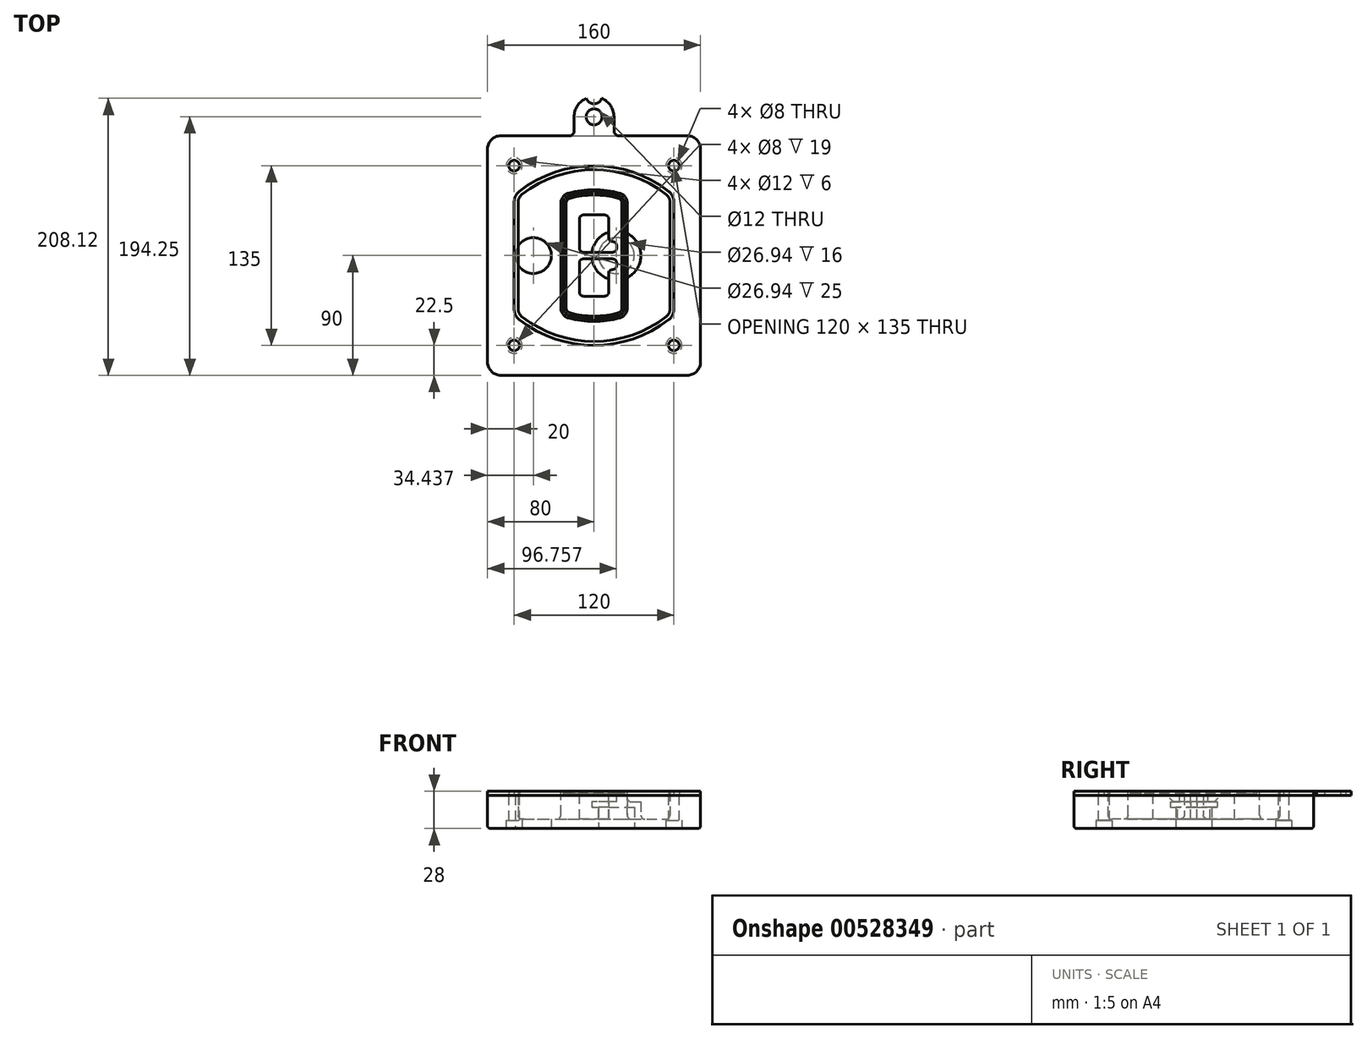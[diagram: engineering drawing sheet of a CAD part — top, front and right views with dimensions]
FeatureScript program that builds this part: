
annotation { "Feature Type Name" : "Feature", "Feature Type Description" : "" }
export const myFeature = defineFeature(function(context is Context, id is Id, definition is map)
    precondition{}
    {
        {
            var Q0;
            Q0=qCreatedBy(makeId("Top.planeOp"),FACE);
            var sketch = newSketch(context, id + "F0", { "sketchPlane" : qUnion([Q0])});
            skPoint(sketch, "E0.rect.middle", {"position": v(0, 0) * mm});
            skLineSegment(sketch, "E1.bottom", {"start": v(-70, -90) * mm, "end": v(70, -90) * mm});
            skLineSegment(sketch, "E1.top", {"start": v(-70, 90) * mm, "end": v(70, 90) * mm});
            skLineSegment(sketch, "E1.left", {"start": v(-80, -80) * mm, "end": v(-80, 80) * mm});
            skLineSegment(sketch, "E1.right", {"start": v(80, -80) * mm, "end": v(80, 80) * mm});
            skLineSegment(sketch, "E2", {"start": v(-80, 90) * mm, "end": v(80, -90) * mm, "construction": true});
            skLineSegment(sketch, "E3", {"start": v(80, 90) * mm, "end": v(-80, -90) * mm, "construction": true});
            skCircle(sketch, "E4", {"center": v(-60, 67.5) * mm, "radius": 4 * mm});
            skCircle(sketch, "E5", {"center": v(60, 67.5) * mm, "radius": 4 * mm});
            skCircle(sketch, "E6", {"center": v(60, -67.5) * mm, "radius": 4 * mm});
            skCircle(sketch, "E7", {"center": v(-60, -67.5) * mm, "radius": 4 * mm});
            skLineSegment(sketch, "E8", {"start": v(-60, 67.5) * mm, "end": v(60, 67.5) * mm, "construction": true});
            skLineSegment(sketch, "E9", {"start": v(60, 67.5) * mm, "end": v(60, -67.5) * mm, "construction": true});
            skLineSegment(sketch, "E10", {"start": v(60, -67.5) * mm, "end": v(-60, -67.5) * mm, "construction": true});
            skLineSegment(sketch, "E11", {"start": v(-60, -67.5) * mm, "end": v(-60, 67.5) * mm, "construction": true});
            skLineSegment(sketch, "E12", {"start": v(-60, 40.3) * mm, "end": v(-60, -40.3) * mm});
            skLineSegment(sketch, "E13", {"start": v(60, 40.3) * mm, "end": v(60, -40.3) * mm});
            skArc(sketch, "E14", {"start": v(56.15, 48.18) * mm, "mid": v(0, 67.5) * mm, "end": v(-56.15, 48.18) * mm});
            skArc(sketch, "E15", {"start": v(-56.15, -48.18) * mm, "mid": v(0, -67.5) * mm, "end": v(56.15, -48.18) * mm});
            skLineSegment(sketch, "E16", {"start": v(-60, 0) * mm, "end": v(60, 0) * mm, "construction": true});
            skPoint(sketch, "E17.visualSharp", {"position": v(-60, -45) * mm});
            skArc(sketch, "E17.filletArc", {"start": v(-60, -40.3) * mm, "mid": v(-58.99, -44.68) * mm, "end": v(-56.15, -48.18) * mm});
            skPoint(sketch, "E18.visualSharp", {"position": v(-60, 45) * mm});
            skArc(sketch, "E18.filletArc", {"start": v(-56.15, 48.18) * mm, "mid": v(-58.99, 44.68) * mm, "end": v(-60, 40.3) * mm});
            skPoint(sketch, "E19.visualSharp", {"position": v(60, 45) * mm});
            skArc(sketch, "E19.filletArc", {"start": v(60, 40.3) * mm, "mid": v(58.99, 44.68) * mm, "end": v(56.15, 48.18) * mm});
            skPoint(sketch, "E20.visualSharp", {"position": v(60, -45) * mm});
            skArc(sketch, "E20.filletArc", {"start": v(56.15, -48.18) * mm, "mid": v(58.99, -44.68) * mm, "end": v(60, -40.3) * mm});
            skPoint(sketch, "E21.visualSharp", {"position": v(-80, 90) * mm});
            skArc(sketch, "E21.filletArc", {"start": v(-70, 90) * mm, "mid": v(-77.07, 87.07) * mm, "end": v(-80, 80) * mm});
            skPoint(sketch, "E22.visualSharp", {"position": v(80, 90) * mm});
            skArc(sketch, "E22.filletArc", {"start": v(80, 80) * mm, "mid": v(77.07, 87.07) * mm, "end": v(70, 90) * mm});
            skPoint(sketch, "E23.visualSharp", {"position": v(80, -90) * mm});
            skArc(sketch, "E23.filletArc", {"start": v(70, -90) * mm, "mid": v(77.07, -87.07) * mm, "end": v(80, -80) * mm});
            skPoint(sketch, "E24.visualSharp", {"position": v(-80, -90) * mm});
            skArc(sketch, "E24.filletArc", {"start": v(-80, -80) * mm, "mid": v(-77.07, -87.07) * mm, "end": v(-70, -90) * mm});
            skArc(sketch, "E25.0", {"start": v(57, 40.3) * mm, "mid": v(56.3, 43.36) * mm, "end": v(54.3, 45.81) * mm});
            skLineSegment(sketch, "E25.1", {"start": v(57, 40.3) * mm, "end": v(57, -40.3) * mm});
            skArc(sketch, "E25.2", {"start": v(54.3, -45.81) * mm, "mid": v(56.3, -43.36) * mm, "end": v(57, -40.3) * mm});
            skArc(sketch, "E25.3", {"start": v(-54.3, -45.81) * mm, "mid": v(0, -64.5) * mm, "end": v(54.3, -45.81) * mm});
            skArc(sketch, "E25.4", {"start": v(-57, -40.3) * mm, "mid": v(-56.3, -43.36) * mm, "end": v(-54.3, -45.81) * mm});
            skArc(sketch, "E25.5", {"start": v(54.3, 45.81) * mm, "mid": v(0, 64.5) * mm, "end": v(-54.3, 45.81) * mm});
            skLineSegment(sketch, "E25.6", {"start": v(-57, 40.3) * mm, "end": v(-57, -40.3) * mm});
            skArc(sketch, "E25.7", {"start": v(-54.3, 45.81) * mm, "mid": v(-56.3, 43.36) * mm, "end": v(-57, 40.3) * mm});
            skArc(sketch, "E26.0", {"start": v(-58.62, 51.33) * mm, "mid": v(-62.58, 46.43) * mm, "end": v(-64, 40.3) * mm});
            skArc(sketch, "E26.1", {"start": v(58.62, 51.33) * mm, "mid": v(0, 71.5) * mm, "end": v(-58.62, 51.33) * mm});
            skArc(sketch, "E26.2", {"start": v(64, 40.3) * mm, "mid": v(62.58, 46.43) * mm, "end": v(58.62, 51.33) * mm});
            skLineSegment(sketch, "E26.3", {"start": v(64, 40.3) * mm, "end": v(64, -40.3) * mm});
            skArc(sketch, "E26.4", {"start": v(58.62, -51.33) * mm, "mid": v(62.58, -46.43) * mm, "end": v(64, -40.3) * mm});
            skLineSegment(sketch, "E26.5", {"start": v(-64, 40.3) * mm, "end": v(-64, -40.3) * mm});
            skArc(sketch, "E26.6", {"start": v(-58.62, -51.33) * mm, "mid": v(0, -71.5) * mm, "end": v(58.62, -51.33) * mm});
            skArc(sketch, "E26.7", {"start": v(-64, -40.3) * mm, "mid": v(-62.58, -46.43) * mm, "end": v(-58.62, -51.33) * mm});
            skSolve(sketch);
        }
        {
            var Q0;
            Q0=makeQuery(id+"F0.imprint","IMPRINT",FACE,{"disambiguationData":[TD([[makeQuery(id+"F0.imprint","IMPRINT",EDGE,{"derivedFrom":sQuery(id+"F0.wireOp",EDGE,"E1.bottom")}),1.0]])]});
            var Q1;
            Q1=makeQuery(id+"F0.imprint","IMPRINT",FACE,{"disambiguationData":[TD([[makeQuery(id+"F0.imprint","IMPRINT",EDGE,{"derivedFrom":sQuery(id+"F0.wireOp",EDGE,"E12")}),1.0]])]});
            var Q2;
            Q2=makeQuery(id+"F0.imprint","IMPRINT",FACE,{"disambiguationData":[TD([[makeQuery(id+"F0.imprint","IMPRINT",EDGE,{"derivedFrom":sQuery(id+"F0.wireOp",EDGE,"E25.0")}),1.0]])]});
            var Q3;
            Q3=makeQuery(id+"F0.imprint","IMPRINT",FACE,{"disambiguationData":[TD([[makeQuery(id+"F0.imprint","IMPRINT",EDGE,{"derivedFrom":sQuery(id+"F0.wireOp",EDGE,"E12")}),-1.0]])]});
            extrude(context, id + "F1", {"entities" : qUnion([Q0, Q1, Q2, Q3]), "oppositeDirection" : true, "depth" : 25 * mm});
        }
        {
            var Q0;
            Q0=makeQuery(id+"F0.imprint","IMPRINT",FACE,{"disambiguationData":[TD([[makeQuery(id+"F0.imprint","IMPRINT",EDGE,{"derivedFrom":sQuery(id+"F0.wireOp",EDGE,"E12")}),1.0]])]});
            extrude(context, id + "F2", {"entities" : qUnion([Q0]), "operationType" : NewBodyOperationType.ADD, "depth" : 3 * mm});
        }
        {
            var Q0;
            Q0=makeQuery(id+"F0.imprint","IMPRINT",FACE,{"disambiguationData":[TD([[makeQuery(id+"F0.imprint","IMPRINT",EDGE,{"derivedFrom":sQuery(id+"F0.wireOp",EDGE,"E25.0")}),1.0]])]});
            extrude(context, id + "F3", {"entities" : qUnion([Q0]), "operationType" : NewBodyOperationType.REMOVE, "oppositeDirection" : true, "depth" : 18 * mm});
        }
        {
            var Q0;
            Q0=makeQuery(id+"F2.opExtrude","CAP_FACE",FACE,{"disambiguationData":[OSD([sQuery(id+"F0.wireOp",EDGE,"E12"),sQuery(id+"F0.wireOp",EDGE,"E13"),sQuery(id+"F0.wireOp",EDGE,"E14"),sQuery(id+"F0.wireOp",EDGE,"E15"),sQuery(id+"F0.wireOp",EDGE,"E17.filletArc"),sQuery(id+"F0.wireOp",EDGE,"E18.filletArc"),sQuery(id+"F0.wireOp",EDGE,"E19.filletArc"),sQuery(id+"F0.wireOp",EDGE,"E20.filletArc"),sQuery(id+"F0.wireOp",EDGE,"E25.0"),sQuery(id+"F0.wireOp",EDGE,"E25.1"),sQuery(id+"F0.wireOp",EDGE,"E25.2"),sQuery(id+"F0.wireOp",EDGE,"E25.3"),sQuery(id+"F0.wireOp",EDGE,"E25.4"),sQuery(id+"F0.wireOp",EDGE,"E25.5"),sQuery(id+"F0.wireOp",EDGE,"E25.6"),sQuery(id+"F0.wireOp",EDGE,"E25.7")])],"isStart":false});
            var sketch = newSketch(context, id + "F4", { "sketchPlane" : qUnion([Q0])});
            skArc(sketch, "E27.0", {"start": v(-19.08, -46.97) * mm, "mid": v(0, -49.5) * mm, "end": v(19.08, -46.97) * mm});
            skArc(sketch, "E28.0", {"start": v(19.08, 46.97) * mm, "mid": v(0, 49.5) * mm, "end": v(-19.08, 46.97) * mm});
            skLineSegment(sketch, "E29", {"start": v(-25, 39.25) * mm, "end": v(-25, -39.25) * mm});
            skLineSegment(sketch, "E30", {"start": v(25, 39.25) * mm, "end": v(25, -39.25) * mm});
            skLineSegment(sketch, "E31", {"start": v(-25, 45.1) * mm, "end": v(25, 45.1) * mm, "construction": true});
            skLineSegment(sketch, "E32", {"start": v(-25, -45.1) * mm, "end": v(25, -45.1) * mm, "construction": true});
            skPoint(sketch, "E33.visualSharp", {"position": v(-25, 45.1) * mm});
            skArc(sketch, "E33.filletArc", {"start": v(-19.08, 46.97) * mm, "mid": v(-23.35, 44.11) * mm, "end": v(-25, 39.25) * mm});
            skPoint(sketch, "E34.visualSharp", {"position": v(25, 45.1) * mm});
            skArc(sketch, "E34.filletArc", {"start": v(25, 39.25) * mm, "mid": v(23.35, 44.11) * mm, "end": v(19.08, 46.97) * mm});
            skPoint(sketch, "E35.visualSharp", {"position": v(25, -45.1) * mm});
            skArc(sketch, "E35.filletArc", {"start": v(19.08, -46.97) * mm, "mid": v(23.35, -44.11) * mm, "end": v(25, -39.25) * mm});
            skPoint(sketch, "E36.visualSharp", {"position": v(-25, -45.1) * mm});
            skArc(sketch, "E36.filletArc", {"start": v(-25, -39.25) * mm, "mid": v(-23.35, -44.11) * mm, "end": v(-19.08, -46.97) * mm});
            skArc(sketch, "E37.0", {"start": v(54.3, 45.81) * mm, "mid": v(0, 64.5) * mm, "end": v(-54.3, 45.81) * mm});
            skArc(sketch, "E37.1", {"start": v(-54.3, 45.81) * mm, "mid": v(-56.3, 43.36) * mm, "end": v(-57, 40.3) * mm});
            skLineSegment(sketch, "E37.2", {"start": v(-57, 40.3) * mm, "end": v(-57, -40.3) * mm});
            skArc(sketch, "E37.3", {"start": v(-57, -40.3) * mm, "mid": v(-56.3, -43.36) * mm, "end": v(-54.3, -45.81) * mm});
            skArc(sketch, "E37.4", {"start": v(-54.3, -45.81) * mm, "mid": v(0, -64.5) * mm, "end": v(54.3, -45.81) * mm});
            skArc(sketch, "E37.5", {"start": v(54.3, -45.81) * mm, "mid": v(56.3, -43.36) * mm, "end": v(57, -40.3) * mm});
            skLineSegment(sketch, "E37.6", {"start": v(57, 40.3) * mm, "end": v(57, -40.3) * mm});
            skArc(sketch, "E37.7", {"start": v(57, 40.3) * mm, "mid": v(56.3, 43.36) * mm, "end": v(54.3, 45.81) * mm});
            skLineSegment(sketch, "E38.0", {"start": v(23, 39.25) * mm, "end": v(23, -39.25) * mm});
            skArc(sketch, "E38.1", {"start": v(18.56, -45.04) * mm, "mid": v(21.76, -42.9) * mm, "end": v(23, -39.25) * mm});
            skArc(sketch, "E38.2", {"start": v(-18.56, -45.04) * mm, "mid": v(0, -47.5) * mm, "end": v(18.56, -45.04) * mm});
            skArc(sketch, "E38.3", {"start": v(-23, -39.25) * mm, "mid": v(-21.76, -42.9) * mm, "end": v(-18.56, -45.04) * mm});
            skLineSegment(sketch, "E38.4", {"start": v(-23, 39.25) * mm, "end": v(-23, -39.25) * mm});
            skArc(sketch, "E38.5", {"start": v(23, 39.25) * mm, "mid": v(21.76, 42.9) * mm, "end": v(18.56, 45.04) * mm});
            skArc(sketch, "E38.6", {"start": v(-18.56, 45.04) * mm, "mid": v(-21.76, 42.9) * mm, "end": v(-23, 39.25) * mm});
            skArc(sketch, "E38.7", {"start": v(18.56, 45.04) * mm, "mid": v(0, 47.5) * mm, "end": v(-18.56, 45.04) * mm});
            skArc(sketch, "E39.0", {"start": v(21, 39.25) * mm, "mid": v(20.18, 41.68) * mm, "end": v(18.04, 43.1) * mm});
            skLineSegment(sketch, "E39.1", {"start": v(21, 39.25) * mm, "end": v(21, -39.25) * mm});
            skArc(sketch, "E39.2", {"start": v(18.04, -43.1) * mm, "mid": v(20.18, -41.68) * mm, "end": v(21, -39.25) * mm});
            skArc(sketch, "E39.3", {"start": v(-18.04, -43.1) * mm, "mid": v(0, -45.5) * mm, "end": v(18.04, -43.1) * mm});
            skArc(sketch, "E39.4", {"start": v(-21, -39.25) * mm, "mid": v(-20.18, -41.68) * mm, "end": v(-18.04, -43.1) * mm});
            skArc(sketch, "E39.5", {"start": v(18.04, 43.1) * mm, "mid": v(0, 45.5) * mm, "end": v(-18.04, 43.1) * mm});
            skLineSegment(sketch, "E39.6", {"start": v(-21, 39.25) * mm, "end": v(-21, -39.25) * mm});
            skArc(sketch, "E39.7", {"start": v(-18.04, 43.1) * mm, "mid": v(-20.18, 41.68) * mm, "end": v(-21, 39.25) * mm});
            skLineSegment(sketch, "E40", {"start": v(-25, 0) * mm, "end": v(25, 0) * mm, "construction": true});
            skLineSegment(sketch, "E41", {"start": v(-11, 5.5) * mm, "end": v(-11, 27.5) * mm});
            skLineSegment(sketch, "E42", {"start": v(-8, 30.5) * mm, "end": v(8, 30.5) * mm});
            skLineSegment(sketch, "E43", {"start": v(11, 27.5) * mm, "end": v(11, 13.5) * mm});
            skLineSegment(sketch, "E44", {"start": v(14, 10.5) * mm, "end": v(14, 10.5) * mm});
            skLineSegment(sketch, "E45", {"start": v(17, 7.5) * mm, "end": v(17, 5.5) * mm});
            skLineSegment(sketch, "E46", {"start": v(14, 2.5) * mm, "end": v(-8, 2.5) * mm});
            skPoint(sketch, "E47.visualSharp", {"position": v(-11, 30.5) * mm});
            skArc(sketch, "E47.filletArc", {"start": v(-8, 30.5) * mm, "mid": v(-10.12, 29.62) * mm, "end": v(-11, 27.5) * mm});
            skPoint(sketch, "E48.visualSharp", {"position": v(11, 30.5) * mm});
            skArc(sketch, "E48.filletArc", {"start": v(11, 27.5) * mm, "mid": v(10.12, 29.62) * mm, "end": v(8, 30.5) * mm});
            skPoint(sketch, "E49.visualSharp", {"position": v(11, 10.5) * mm});
            skArc(sketch, "E49.filletArc", {"start": v(11, 13.5) * mm, "mid": v(11.88, 11.38) * mm, "end": v(14, 10.5) * mm});
            skPoint(sketch, "E50.visualSharp", {"position": v(17, 10.5) * mm});
            skArc(sketch, "E50.filletArc", {"start": v(17, 7.5) * mm, "mid": v(16.12, 9.62) * mm, "end": v(14, 10.5) * mm});
            skPoint(sketch, "E51.visualSharp", {"position": v(17, 2.5) * mm});
            skArc(sketch, "E51.filletArc", {"start": v(14, 2.5) * mm, "mid": v(16.12, 3.38) * mm, "end": v(17, 5.5) * mm});
            skPoint(sketch, "E52.visualSharp", {"position": v(-11, 2.5) * mm});
            skArc(sketch, "E52.filletArc", {"start": v(-11, 5.5) * mm, "mid": v(-10.12, 3.38) * mm, "end": v(-8, 2.5) * mm});
            skLineSegment(sketch, "E53.0.MirrorCS", {"start": v(14, -2.5) * mm, "end": v(-8, -2.5) * mm});
            skArc(sketch, "E54.0.MirrorCS", {"start": v(-11, -5.5) * mm, "mid": v(-10.12, -3.38) * mm, "end": v(-8, -2.5) * mm});
            skLineSegment(sketch, "E55.0.MirrorCS", {"start": v(-11, -5.5) * mm, "end": v(-11, -27.5) * mm});
            skArc(sketch, "E56.0.MirrorCS", {"start": v(-8, -30.5) * mm, "mid": v(-10.12, -29.62) * mm, "end": v(-11, -27.5) * mm});
            skLineSegment(sketch, "E57.0.MirrorCS", {"start": v(-8, -30.5) * mm, "end": v(8, -30.5) * mm});
            skArc(sketch, "E58.0.MirrorCS", {"start": v(11, -27.5) * mm, "mid": v(10.12, -29.62) * mm, "end": v(8, -30.5) * mm});
            skLineSegment(sketch, "E59.0.MirrorCS", {"start": v(11, -27.5) * mm, "end": v(11, -13.5) * mm});
            skArc(sketch, "E60.0.MirrorCS", {"start": v(11, -13.5) * mm, "mid": v(11.88, -11.38) * mm, "end": v(14, -10.5) * mm});
            skArc(sketch, "E61.0.MirrorCS", {"start": v(17, -7.5) * mm, "mid": v(16.12, -9.62) * mm, "end": v(14, -10.5) * mm});
            skLineSegment(sketch, "E62.0.MirrorCS", {"start": v(17, -7.5) * mm, "end": v(17, -5.5) * mm});
            skArc(sketch, "E63.0.MirrorCS", {"start": v(14, -2.5) * mm, "mid": v(16.12, -3.38) * mm, "end": v(17, -5.5) * mm});
            skSolve(sketch);
        }
        {
            var Q0;
            Q0=makeQuery(id+"F4.imprint","IMPRINT",FACE,{"disambiguationData":[TD([[makeQuery(id+"F4.imprint","IMPRINT",EDGE,{"derivedFrom":sQuery(id+"F4.wireOp",EDGE,"E27.0")}),1.0]])]});
            var Q1;
            Q1=makeQuery(id+"F4.imprint","IMPRINT",FACE,{"disambiguationData":[TD([[makeQuery(id+"F4.imprint","IMPRINT",EDGE,{"derivedFrom":sQuery(id+"F4.wireOp",EDGE,"E38.0")}),-1.0]])]});
            var Q2;
            Q2=makeQuery(id+"F4.imprint","IMPRINT",FACE,{"disambiguationData":[TD([[makeQuery(id+"F4.imprint","IMPRINT",EDGE,{"derivedFrom":sQuery(id+"F4.wireOp",EDGE,"E39.0")}),1.0]])]});
            extrude(context, id + "F5", {"entities" : qUnion([Q0, Q1, Q2]), "operationType" : NewBodyOperationType.ADD, "endBound" : BoundingType.UP_TO_NEXT, "oppositeDirection" : true, "depth" : 25 * mm});
        }
        {
            var Q0;
            Q0=makeQuery(id+"F4.imprint","IMPRINT",FACE,{"disambiguationData":[TD([[makeQuery(id+"F4.imprint","IMPRINT",EDGE,{"derivedFrom":sQuery(id+"F4.wireOp",EDGE,"E38.0")}),-1.0]])]});
            extrude(context, id + "F6", {"entities" : qUnion([Q0]), "operationType" : NewBodyOperationType.REMOVE, "oppositeDirection" : true, "depth" : 2 * mm});
        }
        {
            var Q0;
            Q0=makeQuery(id+"F1.opExtrude","CAP_FACE",FACE,{"disambiguationData":[OSD([sQuery(id+"F0.wireOp",EDGE,"E1.bottom"),sQuery(id+"F0.wireOp",EDGE,"E1.top"),sQuery(id+"F0.wireOp",EDGE,"E1.left"),sQuery(id+"F0.wireOp",EDGE,"E1.right"),sQuery(id+"F0.wireOp",EDGE,"E4"),sQuery(id+"F0.wireOp",EDGE,"E5"),sQuery(id+"F0.wireOp",EDGE,"E6"),sQuery(id+"F0.wireOp",EDGE,"E7"),sQuery(id+"F0.wireOp",EDGE,"E21.filletArc"),sQuery(id+"F0.wireOp",EDGE,"E22.filletArc"),sQuery(id+"F0.wireOp",EDGE,"E23.filletArc"),sQuery(id+"F0.wireOp",EDGE,"E24.filletArc")])],"isStart":false});
            var sketch = newSketch(context, id + "F7", { "sketchPlane" : qUnion([Q0])});
            skCircle(sketch, "E64", {"center": v(16.76, 0) * mm, "radius": 13.47 * mm});
            skCircle(sketch, "E65", {"center": v(-45.56, 0) * mm, "radius": 13.47 * mm});
            skLineSegment(sketch, "E66", {"start": v(80, 0) * mm, "end": v(-80, 0) * mm});
            skCircle(sketch, "E67", {"center": v(16.76, 0) * mm, "radius": 18.47 * mm});
            skCircle(sketch, "E68", {"center": v(60, -67.5) * mm, "radius": 6 * mm});
            skCircle(sketch, "E69", {"center": v(-60, -67.5) * mm, "radius": 6 * mm});
            skCircle(sketch, "E70", {"center": v(-60, 67.5) * mm, "radius": 6 * mm});
            skCircle(sketch, "E71", {"center": v(60, 67.5) * mm, "radius": 6 * mm});
            skSolve(sketch);
        }
        {
            var Q0;
            {var subQ1=sQuery(id+"F7.wireOp",EDGE,"E66");var subQ4=sQuery(id+"F7.wireOp",EDGE,"E64");var subQ6=makeQuery(id+"F7.imprint","INTERSECT",VERTEX,{"disambiguationData":[OD(0.0)],"derivedFrom":[subQ4,subQ1]});Q0=makeQuery(id+"F7.imprint","IMPRINT",FACE,{"disambiguationData":[TD([[makeQuery(id+"F7.imprint","IMPRINT",EDGE,{"disambiguationData":[TD([[subQ6,-1.0]])],"derivedFrom":subQ4}),-1.0]])]});}
            var Q1;
            {var subQ0=sQuery(id+"F7.wireOp",EDGE,"E66");var subQ1=sQuery(id+"F7.wireOp",EDGE,"E64");var subQ3=makeQuery(id+"F7.imprint","INTERSECT",VERTEX,{"disambiguationData":[OD(0.0)],"derivedFrom":[subQ1,subQ0]});Q1=makeQuery(id+"F7.imprint","IMPRINT",FACE,{"disambiguationData":[TD([[makeQuery(id+"F7.imprint","IMPRINT",EDGE,{"disambiguationData":[TD([[subQ3,-1.0]])],"derivedFrom":subQ1}),1.0]])]});}
            var Q2;
            {var subQ0=sQuery(id+"F7.wireOp",EDGE,"E66");var subQ1=sQuery(id+"F7.wireOp",EDGE,"E64");var subQ3=makeQuery(id+"F7.imprint","INTERSECT",VERTEX,{"disambiguationData":[OD(0.0)],"derivedFrom":[subQ1,subQ0]});Q2=makeQuery(id+"F7.imprint","IMPRINT",FACE,{"disambiguationData":[TD([[makeQuery(id+"F7.imprint","IMPRINT",EDGE,{"disambiguationData":[TD([[subQ3,1.0]])],"derivedFrom":subQ1}),1.0]])]});}
            var Q3;
            {var subQ1=sQuery(id+"F7.wireOp",EDGE,"E66");var subQ4=sQuery(id+"F7.wireOp",EDGE,"E64");var subQ6=makeQuery(id+"F7.imprint","INTERSECT",VERTEX,{"disambiguationData":[OD(0.0)],"derivedFrom":[subQ4,subQ1]});Q3=makeQuery(id+"F7.imprint","IMPRINT",FACE,{"disambiguationData":[TD([[makeQuery(id+"F7.imprint","IMPRINT",EDGE,{"disambiguationData":[TD([[subQ6,1.0]])],"derivedFrom":subQ4}),-1.0]])]});}
            extrude(context, id + "F8", {"entities" : qUnion([Q0, Q1, Q2, Q3]), "operationType" : NewBodyOperationType.ADD, "oppositeDirection" : true, "depth" : 20 * mm});
        }
        {
            var Q0;
            {var subQ0=sQuery(id+"F7.wireOp",EDGE,"E66");var subQ1=sQuery(id+"F7.wireOp",EDGE,"E64");var subQ3=makeQuery(id+"F7.imprint","INTERSECT",VERTEX,{"disambiguationData":[OD(0.0)],"derivedFrom":[subQ1,subQ0]});Q0=makeQuery(id+"F7.imprint","IMPRINT",FACE,{"disambiguationData":[TD([[makeQuery(id+"F7.imprint","IMPRINT",EDGE,{"disambiguationData":[TD([[subQ3,-1.0]])],"derivedFrom":subQ1}),1.0]])]});}
            var Q1;
            {var subQ0=sQuery(id+"F7.wireOp",EDGE,"E66");var subQ1=sQuery(id+"F7.wireOp",EDGE,"E64");var subQ3=makeQuery(id+"F7.imprint","INTERSECT",VERTEX,{"disambiguationData":[OD(0.0)],"derivedFrom":[subQ1,subQ0]});Q1=makeQuery(id+"F7.imprint","IMPRINT",FACE,{"disambiguationData":[TD([[makeQuery(id+"F7.imprint","IMPRINT",EDGE,{"disambiguationData":[TD([[subQ3,1.0]])],"derivedFrom":subQ1}),1.0]])]});}
            extrude(context, id + "F9", {"entities" : qUnion([Q0, Q1]), "operationType" : NewBodyOperationType.REMOVE, "oppositeDirection" : true, "depth" : 16 * mm});
        }
        {
            var Q0;
            {var subQ0=sQuery(id+"F7.wireOp",EDGE,"E66");var subQ1=sQuery(id+"F7.wireOp",EDGE,"E65");var subQ3=makeQuery(id+"F7.imprint","INTERSECT",VERTEX,{"disambiguationData":[OD(0.0)],"derivedFrom":[subQ1,subQ0]});Q0=makeQuery(id+"F7.imprint","IMPRINT",FACE,{"disambiguationData":[TD([[makeQuery(id+"F7.imprint","IMPRINT",EDGE,{"disambiguationData":[TD([[subQ3,-1.0]])],"derivedFrom":subQ1}),1.0]])]});}
            var Q1;
            {var subQ0=sQuery(id+"F7.wireOp",EDGE,"E66");var subQ1=sQuery(id+"F7.wireOp",EDGE,"E65");var subQ3=makeQuery(id+"F7.imprint","INTERSECT",VERTEX,{"disambiguationData":[OD(0.0)],"derivedFrom":[subQ1,subQ0]});Q1=makeQuery(id+"F7.imprint","IMPRINT",FACE,{"disambiguationData":[TD([[makeQuery(id+"F7.imprint","IMPRINT",EDGE,{"disambiguationData":[TD([[subQ3,1.0]])],"derivedFrom":subQ1}),1.0]])]});}
            extrude(context, id + "F10", {"entities" : qUnion([Q0, Q1]), "operationType" : NewBodyOperationType.REMOVE, "oppositeDirection" : true, "depth" : 25 * mm});
        }
        {
            var Q0;
            Q0=makeQuery(id+"F7.imprint","IMPRINT",FACE,{"disambiguationData":[TD([[makeQuery(id+"F7.imprint","IMPRINT",EDGE,{"derivedFrom":sQuery(id+"F7.wireOp",EDGE,"E68")}),1.0]])]});
            var Q1;
            Q1=makeQuery(id+"F7.imprint","IMPRINT",FACE,{"disambiguationData":[TD([[makeQuery(id+"F7.imprint","IMPRINT",EDGE,{"derivedFrom":makeQuery(id+"F1.opExtrude","CAP_EDGE",EDGE,{"disambiguationData":[OSD([sQuery(id+"F0.wireOp",EDGE,"E5")])],"isStart":false})}),-1.0]])]});
            var Q2;
            Q2=makeQuery(id+"F7.imprint","IMPRINT",FACE,{"disambiguationData":[TD([[makeQuery(id+"F7.imprint","IMPRINT",EDGE,{"derivedFrom":sQuery(id+"F7.wireOp",EDGE,"E69")}),1.0]])]});
            var Q3;
            Q3=makeQuery(id+"F7.imprint","IMPRINT",FACE,{"disambiguationData":[TD([[makeQuery(id+"F7.imprint","IMPRINT",EDGE,{"derivedFrom":makeQuery(id+"F1.opExtrude","CAP_EDGE",EDGE,{"disambiguationData":[OSD([sQuery(id+"F0.wireOp",EDGE,"E4")])],"isStart":false})}),-1.0]])]});
            var Q4;
            Q4=makeQuery(id+"F7.imprint","IMPRINT",FACE,{"disambiguationData":[TD([[makeQuery(id+"F7.imprint","IMPRINT",EDGE,{"derivedFrom":sQuery(id+"F7.wireOp",EDGE,"E70")}),1.0]])]});
            var Q5;
            Q5=makeQuery(id+"F7.imprint","IMPRINT",FACE,{"disambiguationData":[TD([[makeQuery(id+"F7.imprint","IMPRINT",EDGE,{"derivedFrom":makeQuery(id+"F1.opExtrude","CAP_EDGE",EDGE,{"disambiguationData":[OSD([sQuery(id+"F0.wireOp",EDGE,"E7")])],"isStart":false})}),-1.0]])]});
            var Q6;
            Q6=makeQuery(id+"F7.imprint","IMPRINT",FACE,{"disambiguationData":[TD([[makeQuery(id+"F7.imprint","IMPRINT",EDGE,{"derivedFrom":sQuery(id+"F7.wireOp",EDGE,"E71")}),1.0]])]});
            var Q7;
            Q7=makeQuery(id+"F7.imprint","IMPRINT",FACE,{"disambiguationData":[TD([[makeQuery(id+"F7.imprint","IMPRINT",EDGE,{"derivedFrom":makeQuery(id+"F1.opExtrude","CAP_EDGE",EDGE,{"disambiguationData":[OSD([sQuery(id+"F0.wireOp",EDGE,"E6")])],"isStart":false})}),-1.0]])]});
            extrude(context, id + "F11", {"entities" : qUnion([Q0, Q1, Q2, Q3, Q4, Q5, Q6, Q7]), "operationType" : NewBodyOperationType.REMOVE, "oppositeDirection" : true, "depth" : 6 * mm});
        }
        {
            var Q0;
            Q0=makeQuery(id+"F9.boolean.opBoolean","COPY",FACE,{"derivedFrom":makeQuery(id+"F9.opExtrude","CAP_FACE",FACE,{"disambiguationData":[OSD([sQuery(id+"F7.wireOp",EDGE,"E64")])],"isStart":false})});
            var sketch = newSketch(context, id + "F12", { "sketchPlane" : qUnion([Q0])});
            skArc(sketch, "E72.0", {"start": v(11, 17.55) * mm, "mid": v(2.57, 11.82) * mm, "end": v(-1.54, 2.5) * mm});
            skArc(sketch, "E72.1", {"start": v(-1.54, -2.5) * mm, "mid": v(2.57, -11.82) * mm, "end": v(11, -17.55) * mm});
            skLineSegment(sketch, "E73", {"start": v(-1.54, -2.5) * mm, "end": v(14, -2.5) * mm});
            skLineSegment(sketch, "E74.0", {"start": v(14, 2.5) * mm, "end": v(-1.54, 2.5) * mm});
            skArc(sketch, "E74.1", {"start": v(14, 2.5) * mm, "mid": v(16.12, 3.38) * mm, "end": v(17, 5.5) * mm});
            skLineSegment(sketch, "E74.2", {"start": v(17, 7.5) * mm, "end": v(17, 5.5) * mm});
            skArc(sketch, "E74.3", {"start": v(17, 7.5) * mm, "mid": v(16.12, 9.62) * mm, "end": v(14, 10.5) * mm});
            skArc(sketch, "E74.4", {"start": v(11, 13.5) * mm, "mid": v(11.88, 11.38) * mm, "end": v(14, 10.5) * mm});
            skLineSegment(sketch, "E74.5", {"start": v(11, 17.55) * mm, "end": v(11, 13.5) * mm});
            skLineSegment(sketch, "E74.7", {"start": v(14, -2.5) * mm, "end": v(-1.54, -2.5) * mm});
            skArc(sketch, "E74.8", {"start": v(14, -2.5) * mm, "mid": v(16.12, -3.38) * mm, "end": v(17, -5.5) * mm});
            skLineSegment(sketch, "E74.9", {"start": v(17, -7.5) * mm, "end": v(17, -5.5) * mm});
            skArc(sketch, "E74.10", {"start": v(17, -7.5) * mm, "mid": v(16.12, -9.62) * mm, "end": v(14, -10.5) * mm});
            skArc(sketch, "E74.11", {"start": v(11, -13.5) * mm, "mid": v(11.88, -11.38) * mm, "end": v(14, -10.5) * mm});
            skLineSegment(sketch, "E74.12", {"start": v(11, -17.55) * mm, "end": v(11, -13.5) * mm});
            skPoint(sketch, "E75.orphan", {"position": v(11, -27.5) * mm});
            skPoint(sketch, "E76.orphan", {"position": v(-8, -2.5) * mm});
            skPoint(sketch, "E77.orphan", {"position": v(-8, 2.5) * mm});
            skPoint(sketch, "E78.orphan", {"position": v(11, 27.5) * mm});
            skSolve(sketch);
        }
        {
            var Q0;
            {var subQ7=sQuery(id+"F12.wireOp",EDGE,"E72.0");var subQ14=sQuery(id+"F12.wireOp",EDGE,"E72.1");var subQ16=sQuery(id+"F12.wireOp",EDGE,"E74.1");var subQ18=sQuery(id+"F12.wireOp",EDGE,"E74.8");Q0=qUnion([makeQuery(id+"F12.imprint","IMPRINT",FACE,{"disambiguationData":[TD([[makeQuery(id+"F12.imprint","IMPRINT",EDGE,{"derivedFrom":subQ7}),1.0]])]}),makeQuery(id+"F12.imprint","IMPRINT",FACE,{"disambiguationData":[TD([[makeQuery(id+"F12.imprint","IMPRINT",EDGE,{"derivedFrom":subQ14}),1.0]])]}),makeQuery(id+"F12.imprint","IMPRINT",FACE,{"disambiguationData":[TD([[makeQuery(id+"F12.imprint","IMPRINT",EDGE,{"derivedFrom":subQ16}),1.0]])]}),makeQuery(id+"F12.imprint","IMPRINT",FACE,{"disambiguationData":[TD([[makeQuery(id+"F12.imprint","IMPRINT",EDGE,{"derivedFrom":subQ18}),-1.0]])]})]);}
            var Q1;
            Q1=makeQuery(id+"F5.boolean.opBoolean","SPLIT",FACE,{"disambiguationData":[TD([makeQuery(id+"F5.opExtrude","SWEPT_FACE",FACE,{"disambiguationData":[OSD([sQuery(id+"F4.wireOp",EDGE,"E41")])]})])],"derivedFrom":makeQuery(id+"F3.boolean.opBoolean","COPY",FACE,{"derivedFrom":makeQuery(id+"F3.opExtrude","CAP_FACE",FACE,{"disambiguationData":[OSD([sQuery(id+"F0.wireOp",EDGE,"E25.0"),sQuery(id+"F0.wireOp",EDGE,"E25.1"),sQuery(id+"F0.wireOp",EDGE,"E25.2"),sQuery(id+"F0.wireOp",EDGE,"E25.3"),sQuery(id+"F0.wireOp",EDGE,"E25.4"),sQuery(id+"F0.wireOp",EDGE,"E25.5"),sQuery(id+"F0.wireOp",EDGE,"E25.6"),sQuery(id+"F0.wireOp",EDGE,"E25.7")])],"isStart":false})})});
            extrude(context, id + "F13", {"entities" : qUnion([Q0]), "operationType" : NewBodyOperationType.REMOVE, "endBound" : BoundingType.UP_TO_SURFACE, "endBoundEntityFace" : qUnion([Q1]), "depth" : 25 * mm});
        }
        {
            var Q0;
            Q0=makeQuery(id+"F3.boolean.opBoolean","COPY",EDGE,{"derivedFrom":makeQuery(id+"F3.opExtrude","CAP_EDGE",EDGE,{"disambiguationData":[OSD([sQuery(id+"F0.wireOp",EDGE,"E25.6")])],"isStart":false})});
            var Q1;
            Q1=makeQuery(id+"F8.boolean.opBoolean","INTERSECT",EDGE,{"derivedFrom":[makeQuery(id+"F5.opExtrude","SWEPT_FACE",FACE,{"disambiguationData":[OSD([sQuery(id+"F4.wireOp",EDGE,"E30")])]}),makeQuery(id+"F8.opExtrude","CAP_FACE",FACE,{"disambiguationData":[OSD([sQuery(id+"F7.wireOp",EDGE,"E67")])],"isStart":false})]});
            var Q2;
            Q2=makeQuery(id+"F8.boolean.opBoolean","INTERSECT",EDGE,{"disambiguationData":[OD(1.0)],"derivedFrom":[makeQuery(id+"F5.opExtrude","SWEPT_FACE",FACE,{"disambiguationData":[OSD([sQuery(id+"F4.wireOp",EDGE,"E30")])]}),makeQuery(id+"F8.opExtrude","SWEPT_FACE",FACE,{"disambiguationData":[OSD([sQuery(id+"F7.wireOp",EDGE,"E67")])]})]});
            var Q3;
            {var subQ0=sQuery(id+"F4.wireOp",EDGE,"E30");Q3=makeQuery(id+"F8.boolean.opBoolean","SPLIT",EDGE,{"disambiguationData":[TD([makeQuery(id+"F5.opExtrude","SWEPT_FACE",FACE,{"disambiguationData":[OSD([sQuery(id+"F4.wireOp",EDGE,"E35.filletArc")])]})])],"derivedFrom":makeQuery(id+"F5.opExtrude","CAP_EDGE",EDGE,{"disambiguationData":[OSD([subQ0])],"isStart":false})});}
            var Q4;
            {var subQ0=sQuery(id+"F0.wireOp",EDGE,"E25.7");var subQ1=sQuery(id+"F0.wireOp",EDGE,"E25.1");var subQ2=sQuery(id+"F0.wireOp",EDGE,"E25.6");var subQ3=sQuery(id+"F0.wireOp",EDGE,"E25.5");var subQ4=sQuery(id+"F0.wireOp",EDGE,"E25.4");var subQ5=sQuery(id+"F0.wireOp",EDGE,"E25.0");var subQ6=sQuery(id+"F0.wireOp",EDGE,"E25.2");var subQ7=sQuery(id+"F0.wireOp",EDGE,"E25.3");Q4=makeQuery(id+"F8.boolean.opBoolean","INTERSECT",EDGE,{"derivedFrom":[makeQuery(id+"F5.boolean.opBoolean","SPLIT",FACE,{"disambiguationData":[TD([makeQuery(id+"F2.opExtrude","SWEPT_FACE",FACE,{"disambiguationData":[OSD([subQ5])]})])],"derivedFrom":makeQuery(id+"F3.boolean.opBoolean","COPY",FACE,{"derivedFrom":makeQuery(id+"F3.opExtrude","CAP_FACE",FACE,{"disambiguationData":[OSD([subQ5,subQ1,subQ6,subQ7,subQ4,subQ3,subQ2,subQ0])],"isStart":false})})}),makeQuery(id+"F8.opExtrude","SWEPT_FACE",FACE,{"disambiguationData":[OSD([sQuery(id+"F7.wireOp",EDGE,"E67")])]})]});}
            var Q5;
            Q5=makeQuery(id+"F8.boolean.opBoolean","INTERSECT",EDGE,{"disambiguationData":[OD(0.0)],"derivedFrom":[makeQuery(id+"F5.opExtrude","SWEPT_FACE",FACE,{"disambiguationData":[OSD([sQuery(id+"F4.wireOp",EDGE,"E30")])]}),makeQuery(id+"F8.opExtrude","SWEPT_FACE",FACE,{"disambiguationData":[OSD([sQuery(id+"F7.wireOp",EDGE,"E67")])]})]});
            fillet(context, id + "F14", {"entities" : qUnion([Q0, Q1, Q2, Q3, Q4, Q5]), "radius" : 3 * mm, "tangentPropagation" : true, "allowEdgeOverflow" : false});
        }
        {
            var Q0;
            Q0=makeQuery(id+"F1.opExtrude","CAP_EDGE",EDGE,{"disambiguationData":[OSD([sQuery(id+"F0.wireOp",EDGE,"E1.bottom")])],"isStart":false});
            fillet(context, id + "F15", {"entities" : qUnion([Q0]), "radius" : 2 * mm, "tangentPropagation" : true, "allowEdgeOverflow" : false});
        }
        {
            var Q0;
            {var subQ0=sQuery(id+"F0.wireOp",EDGE,"E21.filletArc");var subQ1=sQuery(id+"F0.wireOp",EDGE,"E7");var subQ2=sQuery(id+"F0.wireOp",EDGE,"E6");var subQ3=sQuery(id+"F0.wireOp",EDGE,"E5");var subQ4=sQuery(id+"F0.wireOp",EDGE,"E4");var subQ5=sQuery(id+"F0.wireOp",EDGE,"E22.filletArc");var subQ6=sQuery(id+"F0.wireOp",EDGE,"E1.bottom");var subQ7=sQuery(id+"F0.wireOp",EDGE,"E1.right");var subQ8=sQuery(id+"F0.wireOp",EDGE,"E1.top");var subQ9=sQuery(id+"F0.wireOp",EDGE,"E1.left");var subQ10=sQuery(id+"F0.wireOp",EDGE,"E23.filletArc");var subQ11=sQuery(id+"F0.wireOp",EDGE,"E24.filletArc");Q0=makeQuery(id+"F2.boolean.opBoolean","SPLIT",FACE,{"disambiguationData":[TD([makeQuery(id+"F1.opExtrude","SWEPT_FACE",FACE,{"disambiguationData":[OSD([subQ6])]})])],"derivedFrom":makeQuery(id+"F1.opExtrude","CAP_FACE",FACE,{"disambiguationData":[OSD([subQ6,subQ8,subQ9,subQ7,subQ4,subQ3,subQ2,subQ1,subQ0,subQ5,subQ10,subQ11])],"isStart":true})});}
            var sketch = newSketch(context, id + "F16", { "sketchPlane" : qUnion([Q0])});
            skLineSegment(sketch, "E79", {"start": v(0, 90) * mm, "end": v(0, 120) * mm, "construction": true});
            skPoint(sketch, "E79.endSnap0", {"position": v(0, 90) * mm});
            skLineSegment(sketch, "E80", {"start": v(-15, 108) * mm, "end": v(-15, 120) * mm});
            skLineSegment(sketch, "E81", {"start": v(33, 90) * mm, "end": v(15, 108) * mm});
            skLineSegment(sketch, "E82", {"start": v(15, 108) * mm, "end": v(15, 120) * mm});
            skArc(sketch, "E83", {"start": v(15, 120) * mm, "mid": v(0, 135) * mm, "end": v(-15, 120) * mm});
            skCircle(sketch, "E84", {"center": v(0, 120) * mm, "radius": 6 * mm});
            skLineSegment(sketch, "E85.MirrorCS", {"start": v(15, 92.25) * mm, "end": v(15, 104.25) * mm});
            skLineSegment(sketch, "E86.MirrorCS", {"start": v(-15, 92.25) * mm, "end": v(-15, 104.25) * mm});
            skLineSegment(sketch, "E87.MirrorCS", {"start": v(-33, 74.25) * mm, "end": v(-15, 92.25) * mm});
            skArc(sketch, "E88.MirrorCS", {"start": v(15, 104.25) * mm, "mid": v(0, 119.25) * mm, "end": v(-15, 104.25) * mm});
            skCircle(sketch, "E89.MirrorC", {"center": v(0, 104.25) * mm, "radius": 6 * mm});
            skLineSegment(sketch, "E90.MirrorCS", {"start": v(33, 74.25) * mm, "end": v(15, 92.25) * mm});
            skLineSegment(sketch, "E91.MirrorCS", {"start": v(0, 74.25) * mm, "end": v(0, 104.25) * mm, "construction": true});
            skPoint(sketch, "E92.MirrorP", {"position": v(0, 74.25) * mm});
            skLineSegment(sketch, "E93", {"start": v(-80, 0) * mm, "end": v(80, 0) * mm, "construction": true});
            skLineSegment(sketch, "E94.MirrorCS", {"start": v(33, -90) * mm, "end": v(15, -108) * mm});
            skLineSegment(sketch, "E95.MirrorCS", {"start": v(15, -92.25) * mm, "end": v(15, -104.25) * mm});
            skArc(sketch, "E96.MirrorCS", {"start": v(15, -104.25) * mm, "mid": v(0, -119.25) * mm, "end": v(-15, -104.25) * mm});
            skLineSegment(sketch, "E97.MirrorCS", {"start": v(-15, -92.25) * mm, "end": v(-15, -104.25) * mm});
            skLineSegment(sketch, "E98.MirrorCS", {"start": v(-33, -74.25) * mm, "end": v(-15, -92.25) * mm});
            skCircle(sketch, "E99.MirrorC", {"center": v(0, -120) * mm, "radius": 6 * mm});
            skLineSegment(sketch, "E100.MirrorCS", {"start": v(0, -90) * mm, "end": v(0, -120) * mm, "construction": true});
            skSolve(sketch);
        }
        {
            var Q0;
            Q0=makeQuery(id+"F16.imprint","IMPRINT",FACE,{"disambiguationData":[TD([[makeQuery(id+"F16.imprint","IMPRINT",EDGE,{"derivedFrom":sQuery(id+"F16.wireOp",EDGE,"E86.MirrorCS")}),-1.0]])]});
            var Q1;
            Q1=makeQuery(id+"F16.imprint","IMPRINT",FACE,{"disambiguationData":[TD([[makeQuery(id+"F16.imprint","IMPRINT",EDGE,{"derivedFrom":makeQuery(id+"F1.opExtrude","CAP_EDGE",EDGE,{"disambiguationData":[OSD([sQuery(id+"F0.wireOp",EDGE,"E1.left")])],"isStart":true})}),-1.0]])]});
            var Q2;
            {var subQ0=sQuery(id+"F16.wireOp",EDGE,"E94.MirrorCS");Q2=makeQuery(id+"F16.imprint","IMPRINT",FACE,{"disambiguationData":[TD([[makeQuery(id+"F16.imprint","IMPRINT",EDGE,{"derivedFrom":subQ0}),-1.0]])]});}
            var Q3;
            Q3=makeQuery(id+"F2.opExtrude","CAP_FACE",FACE,{"disambiguationData":[OSD([sQuery(id+"F0.wireOp",EDGE,"E12"),sQuery(id+"F0.wireOp",EDGE,"E13"),sQuery(id+"F0.wireOp",EDGE,"E14"),sQuery(id+"F0.wireOp",EDGE,"E15"),sQuery(id+"F0.wireOp",EDGE,"E17.filletArc"),sQuery(id+"F0.wireOp",EDGE,"E18.filletArc"),sQuery(id+"F0.wireOp",EDGE,"E19.filletArc"),sQuery(id+"F0.wireOp",EDGE,"E20.filletArc"),sQuery(id+"F0.wireOp",EDGE,"E25.0"),sQuery(id+"F0.wireOp",EDGE,"E25.1"),sQuery(id+"F0.wireOp",EDGE,"E25.2"),sQuery(id+"F0.wireOp",EDGE,"E25.3"),sQuery(id+"F0.wireOp",EDGE,"E25.4"),sQuery(id+"F0.wireOp",EDGE,"E25.5"),sQuery(id+"F0.wireOp",EDGE,"E25.6"),sQuery(id+"F0.wireOp",EDGE,"E25.7")])],"isStart":false});
            extrude(context, id + "F17", {"entities" : qUnion([Q0, Q1, Q2]), "endBound" : BoundingType.UP_TO_SURFACE, "depth" : 25 * mm, "endBoundEntityFace" : qUnion([Q3]), "offsetDistance" : 25 * mm});
        }
    });
